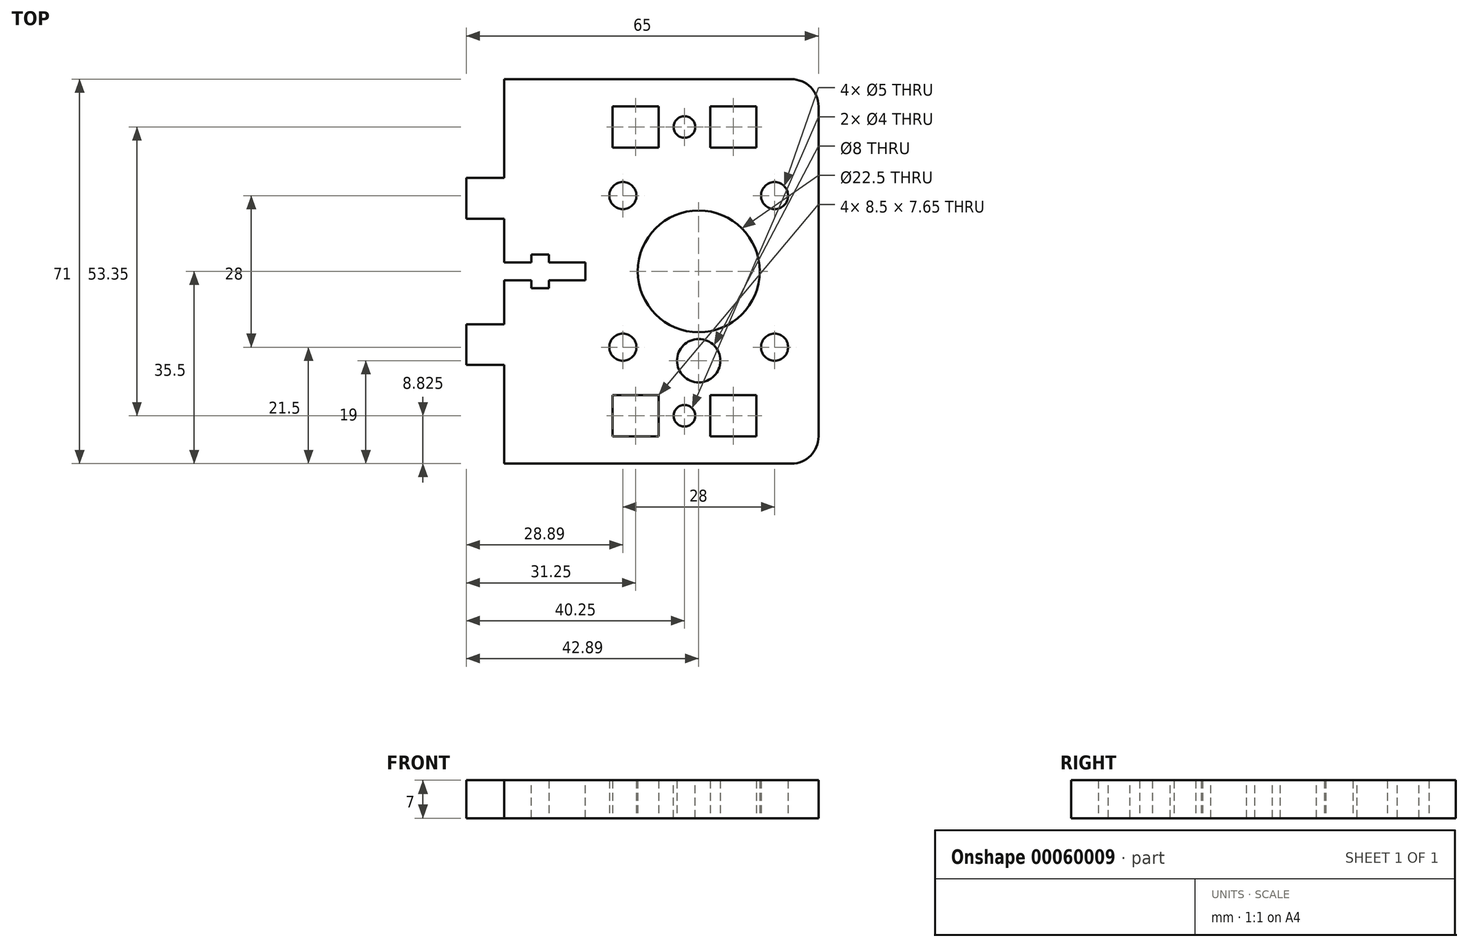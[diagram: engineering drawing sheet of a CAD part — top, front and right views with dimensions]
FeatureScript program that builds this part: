
annotation { "Feature Type Name" : "Feature", "Feature Type Description" : "" }
export const myFeature = defineFeature(function(context is Context, id is Id, definition is map)
    precondition{}
    {
        {
            var Q0;
            Q0=qCreatedBy(makeId("Top.planeOp"),FACE);
            var sketch = newSketch(context, id + "F0", { "sketchPlane" : qUnion([Q0])});
            skLineSegment(sketch, "E0.rect.bottom", {"start": v(-32.5, 35.5) * mm, "end": v(32.5, 35.5) * mm});
            skLineSegment(sketch, "E0.rect.top", {"start": v(-32.5, -35.5) * mm, "end": v(32.5, -35.5) * mm});
            skLineSegment(sketch, "E0.rect.left", {"start": v(-32.5, 35.5) * mm, "end": v(-32.5, -35.5) * mm});
            skLineSegment(sketch, "E0.rect.right", {"start": v(32.5, 35.5) * mm, "end": v(32.5, -35.5) * mm});
            skPoint(sketch, "E0.rect.middle", {"position": v(0, 0) * mm});
            skLineSegment(sketch, "E1.rect.bottom", {"start": v(21, -30.5) * mm, "end": v(12.5, -30.5) * mm});
            skLineSegment(sketch, "E1.rect.top", {"start": v(21, -22.85) * mm, "end": v(12.5, -22.85) * mm});
            skLineSegment(sketch, "E1.rect.left", {"start": v(21, -30.5) * mm, "end": v(21, -22.85) * mm});
            skLineSegment(sketch, "E1.rect.right", {"start": v(12.5, -30.5) * mm, "end": v(12.5, -22.85) * mm});
            skPoint(sketch, "E1.rect.middle", {"position": v(16.75, -26.68) * mm});
            skLineSegment(sketch, "E2.rect.bottom", {"start": v(-5.5, -22.85) * mm, "end": v(3, -22.85) * mm});
            skLineSegment(sketch, "E2.rect.top", {"start": v(-5.5, -30.5) * mm, "end": v(3, -30.5) * mm});
            skLineSegment(sketch, "E2.rect.left", {"start": v(-5.5, -22.85) * mm, "end": v(-5.5, -30.5) * mm});
            skLineSegment(sketch, "E2.rect.right", {"start": v(3, -22.85) * mm, "end": v(3, -30.5) * mm});
            skPoint(sketch, "E2.rect.middle", {"position": v(-1.25, -26.68) * mm});
            skLineSegment(sketch, "E3.MirrorCS", {"start": v(21, 30.5) * mm, "end": v(12.5, 30.5) * mm});
            skPoint(sketch, "E4.MirrorP", {"position": v(16.75, 26.68) * mm});
            skPoint(sketch, "E5.MirrorP", {"position": v(-1.25, 26.68) * mm});
            skLineSegment(sketch, "E6.MirrorCS", {"start": v(3, 22.85) * mm, "end": v(3, 30.5) * mm});
            skLineSegment(sketch, "E7.MirrorCS", {"start": v(-5.5, 22.85) * mm, "end": v(-5.5, 30.5) * mm});
            skLineSegment(sketch, "E8.MirrorCS", {"start": v(-5.5, 30.5) * mm, "end": v(3, 30.5) * mm});
            skLineSegment(sketch, "E9.MirrorCS", {"start": v(-5.5, 22.85) * mm, "end": v(3, 22.85) * mm});
            skLineSegment(sketch, "E10.MirrorCS", {"start": v(12.5, 30.5) * mm, "end": v(12.5, 22.85) * mm});
            skLineSegment(sketch, "E11.MirrorCS", {"start": v(21, 22.85) * mm, "end": v(12.5, 22.85) * mm});
            skLineSegment(sketch, "E12.MirrorCS", {"start": v(21, 30.5) * mm, "end": v(21, 22.85) * mm});
            skSolve(sketch);
        }
        {
            var Q0;
            Q0=makeQuery(id+"F0.imprint","IMPRINT",FACE,{"disambiguationData":[TD([[makeQuery(id+"F0.imprint","IMPRINT",EDGE,{"derivedFrom":sQuery(id+"F0.wireOp",EDGE,"E0.rect.bottom")}),-1.0]])]});
            var sketch = newSketch(context, id + "F1", { "sketchPlane" : qUnion([Q0])});
            skCircle(sketch, "E13", {"center": v(10.39, -16.5) * mm, "radius": 4 * mm});
            skCircle(sketch, "E14", {"center": v(10.4, 0) * mm, "radius": 11.25 * mm});
            skCircle(sketch, "E15", {"center": v(10.4, 0) * mm, "radius": 19.8 * mm, "construction": true});
            skLineSegment(sketch, "E16", {"start": v(24.4, 14) * mm, "end": v(24.4, -14) * mm, "construction": true});
            skLineSegment(sketch, "E17", {"start": v(24.4, -14) * mm, "end": v(-3.6, -14) * mm, "construction": true});
            skLineSegment(sketch, "E18", {"start": v(-3.6, -14) * mm, "end": v(-3.6, 14) * mm, "construction": true});
            skCircle(sketch, "E19", {"center": v(-3.6, 14) * mm, "radius": 2.5 * mm});
            skCircle(sketch, "E20", {"center": v(24.4, 14) * mm, "radius": 2.5 * mm});
            skCircle(sketch, "E21", {"center": v(24.4, -14) * mm, "radius": 2.5 * mm});
            skCircle(sketch, "E22", {"center": v(-3.6, -14) * mm, "radius": 2.5 * mm});
            skLineSegment(sketch, "E23", {"start": v(10.39, -16.5) * mm, "end": v(10.4, 0) * mm, "construction": true});
            skSolve(sketch);
        }
        {
            var Q0;
            Q0=makeQuery(id+"F0.imprint","IMPRINT",FACE,{"disambiguationData":[TD([[makeQuery(id+"F0.imprint","IMPRINT",EDGE,{"derivedFrom":sQuery(id+"F0.wireOp",EDGE,"E0.rect.bottom")}),-1.0]])]});
            extrude(context, id + "F2", {"entities" : qUnion([Q0]), "depth" : 7 * mm});
        }
        {
            var Q0;
            Q0 = qSketchRegion(id + "F1", true);
            extrude(context, id + "F3", {"entities" : qUnion([Q0]), "operationType" : NewBodyOperationType.REMOVE, "depth" : 25 * mm});
        }
        {
            var Q0;
            Q0=makeQuery(id+"F2.opExtrude","CAP_FACE",FACE,{"disambiguationData":[OSD([sQuery(id+"F0.wireOp",EDGE,"E0.rect.bottom"),sQuery(id+"F0.wireOp",EDGE,"E0.rect.top"),sQuery(id+"F0.wireOp",EDGE,"E0.rect.left"),sQuery(id+"F0.wireOp",EDGE,"E0.rect.right"),sQuery(id+"F0.wireOp",EDGE,"E1.rect.bottom"),sQuery(id+"F0.wireOp",EDGE,"E1.rect.top"),sQuery(id+"F0.wireOp",EDGE,"E1.rect.left"),sQuery(id+"F0.wireOp",EDGE,"E1.rect.right"),sQuery(id+"F0.wireOp",EDGE,"E2.rect.bottom"),sQuery(id+"F0.wireOp",EDGE,"E2.rect.top"),sQuery(id+"F0.wireOp",EDGE,"E2.rect.left"),sQuery(id+"F0.wireOp",EDGE,"E2.rect.right"),sQuery(id+"F0.wireOp",EDGE,"E3.MirrorCS"),sQuery(id+"F0.wireOp",EDGE,"E6.MirrorCS"),sQuery(id+"F0.wireOp",EDGE,"E7.MirrorCS"),sQuery(id+"F0.wireOp",EDGE,"E8.MirrorCS"),sQuery(id+"F0.wireOp",EDGE,"E9.MirrorCS"),sQuery(id+"F0.wireOp",EDGE,"E10.MirrorCS"),sQuery(id+"F0.wireOp",EDGE,"E11.MirrorCS"),sQuery(id+"F0.wireOp",EDGE,"E12.MirrorCS")])],"isStart":false});
            var sketch = newSketch(context, id + "F4", { "sketchPlane" : qUnion([Q0])});
            skPoint(sketch, "E24.centerSnap0", {"position": v(12.5, 26.68) * mm});
            skLineSegment(sketch, "E25", {"start": v(3, 26.68) * mm, "end": v(12.5, 26.68) * mm, "construction": true});
            skCircle(sketch, "E26", {"center": v(7.75, 26.68) * mm, "radius": 2 * mm});
            skCircle(sketch, "E27.MirrorC", {"center": v(7.75, -26.68) * mm, "radius": 2 * mm});
            skSolve(sketch);
        }
        {
            var Q0;
            Q0 = qSketchRegion(id + "F4", true);
            extrude(context, id + "F5", {"entities" : qUnion([Q0]), "operationType" : NewBodyOperationType.REMOVE, "endBound" : BoundingType.THROUGH_ALL, "oppositeDirection" : true, "depth" : 25 * mm});
        }
        {
            var Q0;
            Q0=makeQuery(id+"F2.opExtrude","CAP_FACE",FACE,{"disambiguationData":[OSD([sQuery(id+"F0.wireOp",EDGE,"E0.rect.bottom"),sQuery(id+"F0.wireOp",EDGE,"E0.rect.top"),sQuery(id+"F0.wireOp",EDGE,"E0.rect.left"),sQuery(id+"F0.wireOp",EDGE,"E0.rect.right"),sQuery(id+"F0.wireOp",EDGE,"E1.rect.bottom"),sQuery(id+"F0.wireOp",EDGE,"E1.rect.top"),sQuery(id+"F0.wireOp",EDGE,"E1.rect.left"),sQuery(id+"F0.wireOp",EDGE,"E1.rect.right"),sQuery(id+"F0.wireOp",EDGE,"E2.rect.bottom"),sQuery(id+"F0.wireOp",EDGE,"E2.rect.top"),sQuery(id+"F0.wireOp",EDGE,"E2.rect.left"),sQuery(id+"F0.wireOp",EDGE,"E2.rect.right"),sQuery(id+"F0.wireOp",EDGE,"E3.MirrorCS"),sQuery(id+"F0.wireOp",EDGE,"E6.MirrorCS"),sQuery(id+"F0.wireOp",EDGE,"E7.MirrorCS"),sQuery(id+"F0.wireOp",EDGE,"E8.MirrorCS"),sQuery(id+"F0.wireOp",EDGE,"E9.MirrorCS"),sQuery(id+"F0.wireOp",EDGE,"E10.MirrorCS"),sQuery(id+"F0.wireOp",EDGE,"E11.MirrorCS"),sQuery(id+"F0.wireOp",EDGE,"E12.MirrorCS")])],"isStart":false});
            var sketch = newSketch(context, id + "F6", { "sketchPlane" : qUnion([Q0])});
            skLineSegment(sketch, "E28.bottom", {"start": v(-32.5, 35.5) * mm, "end": v(-25.5, 35.5) * mm});
            skLineSegment(sketch, "E28.top", {"start": v(-32.5, 17.25) * mm, "end": v(-25.5, 17.25) * mm});
            skLineSegment(sketch, "E28.left", {"start": v(-32.5, 35.5) * mm, "end": v(-32.5, 17.25) * mm});
            skLineSegment(sketch, "E28.right", {"start": v(-25.5, 35.5) * mm, "end": v(-25.5, 17.25) * mm});
            skLineSegment(sketch, "E29.MirrorCS", {"start": v(-25.5, -35.5) * mm, "end": v(-25.5, -17.25) * mm});
            skLineSegment(sketch, "E30.MirrorCS", {"start": v(-32.5, -35.5) * mm, "end": v(-32.5, -17.25) * mm});
            skLineSegment(sketch, "E31.MirrorCS", {"start": v(-32.5, -35.5) * mm, "end": v(-25.5, -35.5) * mm});
            skLineSegment(sketch, "E32.MirrorCS", {"start": v(-32.5, -17.25) * mm, "end": v(-25.5, -17.25) * mm});
            skLineSegment(sketch, "E33.bottom", {"start": v(-32.5, 9.75) * mm, "end": v(-25.5, 9.75) * mm});
            skLineSegment(sketch, "E33.top", {"start": v(-32.5, -9.75) * mm, "end": v(-25.5, -9.75) * mm});
            skLineSegment(sketch, "E33.left", {"start": v(-32.5, 9.75) * mm, "end": v(-32.5, -9.75) * mm});
            skLineSegment(sketch, "E33.right", {"start": v(-25.5, 9.75) * mm, "end": v(-25.5, -9.75) * mm});
            skSolve(sketch);
        }
        {
            var Q0;
            Q0 = qSketchRegion(id + "F6", true);
            extrude(context, id + "F7", {"entities" : qUnion([Q0]), "operationType" : NewBodyOperationType.REMOVE, "endBound" : BoundingType.THROUGH_ALL, "oppositeDirection" : true, "depth" : 25 * mm});
        }
        {
            var Q0;
            Q0=makeQuery(id+"F2.opExtrude","CAP_FACE",FACE,{"disambiguationData":[OSD([sQuery(id+"F0.wireOp",EDGE,"E0.rect.bottom"),sQuery(id+"F0.wireOp",EDGE,"E0.rect.top"),sQuery(id+"F0.wireOp",EDGE,"E0.rect.left"),sQuery(id+"F0.wireOp",EDGE,"E0.rect.right"),sQuery(id+"F0.wireOp",EDGE,"E1.rect.bottom"),sQuery(id+"F0.wireOp",EDGE,"E1.rect.top"),sQuery(id+"F0.wireOp",EDGE,"E1.rect.left"),sQuery(id+"F0.wireOp",EDGE,"E1.rect.right"),sQuery(id+"F0.wireOp",EDGE,"E2.rect.bottom"),sQuery(id+"F0.wireOp",EDGE,"E2.rect.top"),sQuery(id+"F0.wireOp",EDGE,"E2.rect.left"),sQuery(id+"F0.wireOp",EDGE,"E2.rect.right"),sQuery(id+"F0.wireOp",EDGE,"E3.MirrorCS"),sQuery(id+"F0.wireOp",EDGE,"E6.MirrorCS"),sQuery(id+"F0.wireOp",EDGE,"E7.MirrorCS"),sQuery(id+"F0.wireOp",EDGE,"E8.MirrorCS"),sQuery(id+"F0.wireOp",EDGE,"E9.MirrorCS"),sQuery(id+"F0.wireOp",EDGE,"E10.MirrorCS"),sQuery(id+"F0.wireOp",EDGE,"E11.MirrorCS"),sQuery(id+"F0.wireOp",EDGE,"E12.MirrorCS")])],"isStart":false});
            var sketch = newSketch(context, id + "F8", { "sketchPlane" : qUnion([Q0])});
            skLineSegment(sketch, "E34.rect.bottom", {"start": v(-40.5, 1.62) * mm, "end": v(-10.5, 1.63) * mm});
            skLineSegment(sketch, "E34.rect.top", {"start": v(-40.5, -1.62) * mm, "end": v(-10.5, -1.62) * mm});
            skLineSegment(sketch, "E34.rect.left", {"start": v(-40.5, 1.62) * mm, "end": v(-40.5, -1.63) * mm});
            skLineSegment(sketch, "E34.rect.right", {"start": v(-10.5, 1.62) * mm, "end": v(-10.5, -1.63) * mm});
            skPoint(sketch, "E34.rect.middle", {"position": v(-25.5, 0) * mm});
            skSolve(sketch);
        }
        {
            var Q0;
            {var subQ26=sQuery(id+"F8.wireOp",EDGE,"E34.rect.right");Q0=makeQuery(id+"F8.imprint","IMPRINT",FACE,{"disambiguationData":[TD([[makeQuery(id+"F8.imprint","IMPRINT",EDGE,{"derivedFrom":subQ26}),1.0]])]});}
            var sketch = newSketch(context, id + "F9", { "sketchPlane" : qUnion([Q0])});
            skLineSegment(sketch, "E35.rect.bottom", {"start": v(-17.25, 3.12) * mm, "end": v(-20.5, 3.12) * mm});
            skLineSegment(sketch, "E35.rect.top", {"start": v(-17.25, -3.12) * mm, "end": v(-20.5, -3.12) * mm});
            skLineSegment(sketch, "E35.rect.left", {"start": v(-17.25, 3.12) * mm, "end": v(-17.25, -3.12) * mm});
            skLineSegment(sketch, "E35.rect.right", {"start": v(-20.5, 3.12) * mm, "end": v(-20.5, -3.12) * mm});
            skPoint(sketch, "E35.rect.middle", {"position": v(-18.87, 0) * mm});
            skSolve(sketch);
        }
        {
            var Q0;
            Q0 = qSketchRegion(id + "F8", true);
            var Q1;
            Q1 = qSketchRegion(id + "F9", true);
            extrude(context, id + "F10", {"entities" : qUnion([Q0, Q1]), "operationType" : NewBodyOperationType.REMOVE, "endBound" : BoundingType.THROUGH_ALL, "oppositeDirection" : true, "depth" : 25 * mm});
        }
        {
            var Q0;
            Q0=makeQuery(id+"F2.opExtrude","SWEPT_EDGE",EDGE,{"disambiguationData":[OSD([sQuery(id+"F0.wireOp",EDGE,"E0.rect.top"),sQuery(id+"F0.wireOp",EDGE,"E0.rect.right")])]});
            var Q1;
            Q1=makeQuery(id+"F2.opExtrude","SWEPT_EDGE",EDGE,{"disambiguationData":[OSD([sQuery(id+"F0.wireOp",EDGE,"E0.rect.bottom"),sQuery(id+"F0.wireOp",EDGE,"E0.rect.right")])]});
            fillet(context, id + "F11", {"entities" : qUnion([Q0, Q1]), "radius" : 5 * mm, "tangentPropagation" : true, "allowEdgeOverflow" : false});
        }
    });
